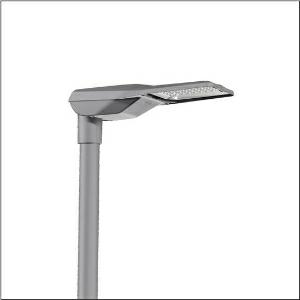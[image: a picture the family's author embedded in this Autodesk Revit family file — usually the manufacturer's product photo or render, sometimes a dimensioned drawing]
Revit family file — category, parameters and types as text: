
# Revit family: streetlight_sl_21_iq_mini___st1_0a_5xe2d61d08hb_7283
name_source: partatom
category: Lighting Fixtures
units: mm (PartAtom-declared; Revit-internal decimal feet)

## family parameters
Cut with Voids When Loaded = No
Host = Face
Light Source = No
Part Type = Normal
Room Calculation Point = No
Round Connector Dimension = Use Diameter
Shared = No

## types (1)
- --- (1 x LED, 8480 lm, 70.9 W, 2700K)
    Apparent Load = 71 VA
    CIE Flux Codes = 37 72 97 100 100
    Color Rendering = 70
    Color Temperature = 2700K
    Default Elevation = 1800 mm
    Description = Streetlight SL 21 iQ mini, mast luminaire, primary light control with lens, of PMMA, primary optical cover: cover, of toughened safety glass, transparent, light distribution: ST1.0a, light emission: direct distribution, primary light characteristic: asymmetric, installation type: post-top, side-entry, LED, High Power LED, rated luminous flux: 8.480lm, luminous efficacy: 120lm/W, light colour: 727, colour temperature: 2700K, control gear: iQ-Comfort, control: Auto-Match, Temp-Guard, Lumen-Switch, Night-Set, Smart-Wire, Light-Fading, Desk-Remote (wireless, voltage-free reading and setting of iQ features in the workshop via application-optimized NFC function/RFID function), optimised constant luminous flux control (CLO 2.0), pre-setting: linear dimming characteristic, mains connection: 220..240V, AC, 50/60Hz, start of lifetime: 71W, end of service life: 75W, reduction: 31W, luminaire housing, of diecast aluminium, powder-coated, SITECO metallic grey (DB 702S), corrosivity category C5 high according to DIN EN ISO 12944, please order mast flange separately, inclination adjustable: 0°, 5°, 10°, 15°, sealing non-destructively replaceable, multi-level sealing system, length: 628mm, width: 235mm, height: 110mm, mast flange for spigot size: 42mm (side-entry): 5XC10008XM4, 60/48mm (side-entry/post-top): 5XC10108XM2, 76/60mm (side-entry/post-top): 5XC10108XM1, mounting height: 4..8m, protection rating (complete): IP66, insulation class (complete): insulation class II (safety insulation), certification: CE, ENEC, ENEC+, VDE, impact resistance: IK10, permissible operating ambient temperature for outdoor applications: -40..+50°C, standard-compliant lighting for roads and squares, packaging unit: 1 piece

Light Distribution: ST1.0a
    Height = 110 mm
    Lamp = 1 x LED
    Lamp Light Flux = 8480 lm
    Lamp Power = 70.9 W
    Lamp count = 1
    Length = 625 mm
    Luminous efficacy = 120 lm/W
    Manufacturer = Siteco
    ModVariant = No
    Model = 5XE2D61D08HB
    Number of Poles = 1
    OnlyDefault = Yes
    Power Factor = 1
    Product Name = Streetlight SL 21 iQ mini | ST1.0a
    Product group = mast luminaire | pylon top
    ProductGroupID = 6100
    Protection Class = Protection class II
    Protection Degree = IP 66
    RLX_Detail_Level = 1
    RLX_Emergency_Light_Flux = 0 lm
    RLX_Emergency_Type = 0
    RLX_Emergency_Type_DB = No
    RlxData = <blob elided: 26237 chars, md5=72d194ab>
    Socket = socket
    Standby Power = 0 W
    System Light Flux = 8480 lm
    System Power = 71 W
    Type Comments = factory setting: luminous flux: 100 % | dim-lin: 254 | 711 mA
    Type Image = l_1003519.jpg
    URL = http://relux.com
    VarID = @adj_157717
    Voltage = 0 V
    Weight = 0.00 kg
    Width = 234 mm

## geometry (parser evidence)
native form markers: Blend x4, Sweep x8
no freeform markers — native parametric forms only
